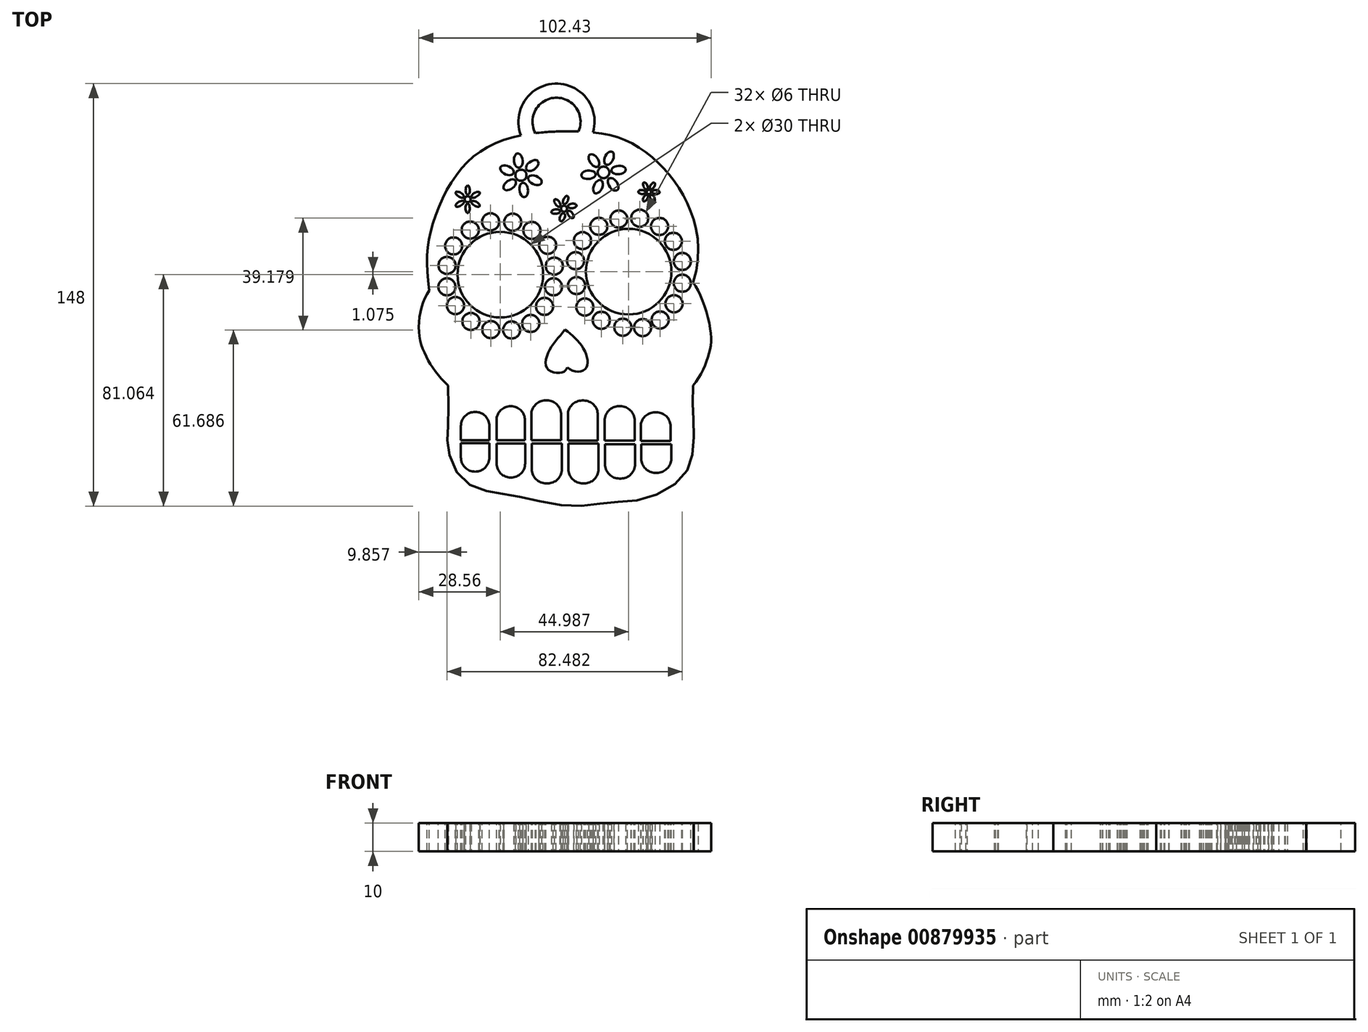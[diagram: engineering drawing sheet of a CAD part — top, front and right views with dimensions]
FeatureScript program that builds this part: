
annotation { "Feature Type Name" : "Feature", "Feature Type Description" : "" }
export const myFeature = defineFeature(function(context is Context, id is Id, definition is map)
    precondition{}
    {
        {
            var Q0;
            Q0=qCreatedBy(makeId("Top.planeOp"),FACE);
            var sketch = newSketch(context, id + "F0", { "sketchPlane" : qUnion([Q0])});
            skFitSpline(sketch, "E0", {"points": [v(-51.65, 30.7) * mm, v(-51.37, 50.55) * mm, v(-42.58, 70.68) * mm, v(-27.27, 82.88) * mm, v(-3.45, 86.56) * mm, v(15.55, 84.01) * mm, v(29.16, 74.94) * mm, v(39.37, 59.9) * mm, v(40.79, 33.54) * mm], "startDerivative": vector(-28.64, 201.5) * mm, "endDerivative": vector(-70.43, -226.16) * mm});
            skFitSpline(sketch, "E1", {"points": [v(-51.65, 30.7) * mm, v(-55.34, 17.94) * mm, v(-52.5, 7.17) * mm, v(-45.13, -2.47) * mm], "startDerivative": vector(-19.76, -24.65) * mm, "endDerivative": vector(28.6, -26.74) * mm});
            skFitSpline(sketch, "E2", {"points": [v(40.79, 33.54) * mm, v(46.74, 17.66) * mm, v(46.18, 8.02) * mm, v(40.79, -2.47) * mm], "startDerivative": vector(20.4, -25) * mm, "endDerivative": vector(-24.31, -27.97) * mm});
            skFitSpline(sketch, "E3", {"points": [v(-45.13, -2.47) * mm, v(-45.13, -17.5) * mm, v(-45.13, -24.6) * mm, v(-40.03, -35.37) * mm, v(-29.53, -39.9) * mm, v(-19.33, -41.6) * mm, v(-2.6, -44.72) * mm, v(10.73, -43.6) * mm, v(23.77, -42.17) * mm, v(37.1, -34.52) * mm, v(40.79, -24.88) * mm, v(40.79, -13.25) * mm, v(40.79, -2.47) * mm], "startDerivative": vector(7.8, -164.11) * mm, "endDerivative": vector(8.57, 179.66) * mm});
            skSolve(sketch);
        }
        {
            var Q0;
            Q0 = qSketchRegion(id + "F0", true);
            extrude(context, id + "F1", {"entities" : qUnion([Q0]), "oppositeDirection" : true, "depth" : 10 * mm, "offsetDistance" : 25.4 * mm});
        }
        {
            var Q0;
            Q0=makeQuery(id+"F1.opExtrude","CAP_FACE",FACE,{"disambiguationData":[OSD([sQuery(id+"F0.wireOp",EDGE,"E0"),sQuery(id+"F0.wireOp",EDGE,"E1"),sQuery(id+"F0.wireOp",EDGE,"E2"),sQuery(id+"F0.wireOp",EDGE,"E3")])],"isStart":true});
            var sketch = newSketch(context, id + "F2", { "sketchPlane" : qUnion([Q0])});
            skCircle(sketch, "E4", {"center": v(-26.78, 36.3) * mm, "radius": 15 * mm});
            skCircle(sketch, "E5", {"center": v(18.2, 37.38) * mm, "radius": 15 * mm});
            skSolve(sketch);
        }
        {
            var Q0;
            Q0 = qSketchRegion(id + "F2", true);
            extrude(context, id + "F3", {"entities" : qUnion([Q0]), "operationType" : NewBodyOperationType.REMOVE, "oppositeDirection" : true, "depth" : 20 * mm, "offsetDistance" : 25 * mm});
        }
        {
            var Q0;
            Q0=makeQuery(id+"F1.opExtrude","CAP_FACE",FACE,{"disambiguationData":[OSD([sQuery(id+"F0.wireOp",EDGE,"E0"),sQuery(id+"F0.wireOp",EDGE,"E1"),sQuery(id+"F0.wireOp",EDGE,"E2"),sQuery(id+"F0.wireOp",EDGE,"E3")])],"isStart":true});
            var sketch = newSketch(context, id + "F4", { "sketchPlane" : qUnion([Q0])});
            skLineSegment(sketch, "E6.bottom", {"start": v(-40.6, -11.76) * mm, "end": v(-30.6, -11.76) * mm});
            skLineSegment(sketch, "E6.top", {"start": v(-40.6, -21.76) * mm, "end": v(-30.6, -21.76) * mm});
            skLineSegment(sketch, "E6.left", {"start": v(-40.6, -11.76) * mm, "end": v(-40.6, -21.76) * mm});
            skLineSegment(sketch, "E6.right", {"start": v(-30.6, -11.76) * mm, "end": v(-30.6, -21.76) * mm});
            skSolve(sketch);
        }
        {
            var Q0;
            Q0 = qSketchRegion(id + "F4", true);
            extrude(context, id + "F5", {"entities" : qUnion([Q0]), "operationType" : NewBodyOperationType.REMOVE, "oppositeDirection" : true, "depth" : 20 * mm, "offsetDistance" : 25 * mm});
        }
        {
            var Q0;
            Q0=makeQuery(id+"F1.opExtrude","CAP_FACE",FACE,{"disambiguationData":[OSD([sQuery(id+"F0.wireOp",EDGE,"E0"),sQuery(id+"F0.wireOp",EDGE,"E1"),sQuery(id+"F0.wireOp",EDGE,"E2"),sQuery(id+"F0.wireOp",EDGE,"E3")])],"isStart":true});
            var sketch = newSketch(context, id + "F6", { "sketchPlane" : qUnion([Q0])});
            skLineSegment(sketch, "E7.bottom", {"start": v(-28.12, -9.76) * mm, "end": v(-18.12, -9.76) * mm});
            skLineSegment(sketch, "E7.top", {"start": v(-28.12, -21.76) * mm, "end": v(-18.12, -21.76) * mm});
            skLineSegment(sketch, "E7.left", {"start": v(-28.12, -9.76) * mm, "end": v(-28.12, -21.76) * mm});
            skLineSegment(sketch, "E7.right", {"start": v(-18.12, -9.76) * mm, "end": v(-18.12, -21.76) * mm});
            skSolve(sketch);
        }
        {
            var Q0;
            Q0 = qSketchRegion(id + "F6", true);
            extrude(context, id + "F7", {"entities" : qUnion([Q0]), "operationType" : NewBodyOperationType.REMOVE, "oppositeDirection" : true, "depth" : 20 * mm, "offsetDistance" : 25 * mm});
        }
        {
            var Q0;
            Q0=makeQuery(id+"F1.opExtrude","CAP_FACE",FACE,{"disambiguationData":[OSD([sQuery(id+"F0.wireOp",EDGE,"E0"),sQuery(id+"F0.wireOp",EDGE,"E1"),sQuery(id+"F0.wireOp",EDGE,"E2"),sQuery(id+"F0.wireOp",EDGE,"E3")])],"isStart":true});
            var sketch = newSketch(context, id + "F8", { "sketchPlane" : qUnion([Q0])});
            skLineSegment(sketch, "E8.bottom", {"start": v(-15.92, -7.76) * mm, "end": v(-5.42, -7.76) * mm});
            skLineSegment(sketch, "E8.top", {"start": v(-15.92, -21.76) * mm, "end": v(-5.42, -21.76) * mm});
            skLineSegment(sketch, "E8.left", {"start": v(-15.92, -7.76) * mm, "end": v(-15.92, -21.76) * mm});
            skLineSegment(sketch, "E8.right", {"start": v(-5.42, -7.76) * mm, "end": v(-5.42, -21.76) * mm});
            skSolve(sketch);
        }
        {
            var Q0;
            Q0 = qSketchRegion(id + "F8", true);
            extrude(context, id + "F9", {"entities" : qUnion([Q0]), "operationType" : NewBodyOperationType.REMOVE, "oppositeDirection" : true, "depth" : 20 * mm, "offsetDistance" : 25 * mm});
        }
        {
            var Q0;
            Q0=makeQuery(id+"F1.opExtrude","CAP_FACE",FACE,{"disambiguationData":[OSD([sQuery(id+"F0.wireOp",EDGE,"E0"),sQuery(id+"F0.wireOp",EDGE,"E1"),sQuery(id+"F0.wireOp",EDGE,"E2"),sQuery(id+"F0.wireOp",EDGE,"E3")])],"isStart":true});
            var sketch = newSketch(context, id + "F10", { "sketchPlane" : qUnion([Q0])});
            skLineSegment(sketch, "E9.bottom", {"start": v(-3.1, -7.78) * mm, "end": v(7.4, -7.78) * mm});
            skLineSegment(sketch, "E9.top", {"start": v(-3.1, -21.78) * mm, "end": v(7.4, -21.78) * mm});
            skLineSegment(sketch, "E9.left", {"start": v(-3.1, -7.78) * mm, "end": v(-3.1, -21.78) * mm});
            skLineSegment(sketch, "E9.right", {"start": v(7.4, -7.78) * mm, "end": v(7.4, -21.78) * mm});
            skSolve(sketch);
        }
        {
            var Q0;
            Q0 = qSketchRegion(id + "F10", true);
            extrude(context, id + "F11", {"entities" : qUnion([Q0]), "operationType" : NewBodyOperationType.REMOVE, "oppositeDirection" : true, "depth" : 20 * mm, "offsetDistance" : 25 * mm});
        }
        {
            var Q0;
            Q0=makeQuery(id+"F1.opExtrude","CAP_FACE",FACE,{"disambiguationData":[OSD([sQuery(id+"F0.wireOp",EDGE,"E0"),sQuery(id+"F0.wireOp",EDGE,"E1"),sQuery(id+"F0.wireOp",EDGE,"E2"),sQuery(id+"F0.wireOp",EDGE,"E3")])],"isStart":true});
            var sketch = newSketch(context, id + "F12", { "sketchPlane" : qUnion([Q0])});
            skPoint(sketch, "E10.oppositeSnap0", {"position": v(2.15, -21.78) * mm});
            skLineSegment(sketch, "E10.bottom", {"start": v(9.8, -9.78) * mm, "end": v(20.3, -9.78) * mm});
            skLineSegment(sketch, "E10.top", {"start": v(9.8, -21.78) * mm, "end": v(20.3, -21.78) * mm});
            skLineSegment(sketch, "E10.left", {"start": v(9.8, -9.78) * mm, "end": v(9.8, -21.78) * mm});
            skLineSegment(sketch, "E10.right", {"start": v(20.3, -9.78) * mm, "end": v(20.3, -21.78) * mm});
            skSolve(sketch);
        }
        {
            var Q0;
            Q0 = qSketchRegion(id + "F12", true);
            extrude(context, id + "F13", {"entities" : qUnion([Q0]), "operationType" : NewBodyOperationType.REMOVE, "oppositeDirection" : true, "depth" : 20 * mm, "offsetDistance" : 25 * mm});
        }
        {
            var Q0;
            Q0=makeQuery(id+"F1.opExtrude","CAP_FACE",FACE,{"disambiguationData":[OSD([sQuery(id+"F0.wireOp",EDGE,"E0"),sQuery(id+"F0.wireOp",EDGE,"E1"),sQuery(id+"F0.wireOp",EDGE,"E2"),sQuery(id+"F0.wireOp",EDGE,"E3")])],"isStart":true});
            var sketch = newSketch(context, id + "F14", { "sketchPlane" : qUnion([Q0])});
            skLineSegment(sketch, "E11.bottom", {"start": v(22.43, -11.91) * mm, "end": v(32.93, -11.91) * mm});
            skLineSegment(sketch, "E11.top", {"start": v(22.43, -21.91) * mm, "end": v(32.93, -21.91) * mm});
            skLineSegment(sketch, "E11.left", {"start": v(22.43, -11.91) * mm, "end": v(22.43, -21.91) * mm});
            skLineSegment(sketch, "E11.right", {"start": v(32.93, -11.91) * mm, "end": v(32.93, -21.91) * mm});
            skSolve(sketch);
        }
        {
            var Q0;
            Q0 = qSketchRegion(id + "F14", true);
            extrude(context, id + "F15", {"entities" : qUnion([Q0]), "operationType" : NewBodyOperationType.REMOVE, "oppositeDirection" : true, "depth" : 20 * mm, "offsetDistance" : 25 * mm});
        }
        {
            var Q0;
            Q0=makeQuery(id+"F1.opExtrude","CAP_FACE",FACE,{"disambiguationData":[OSD([sQuery(id+"F0.wireOp",EDGE,"E0"),sQuery(id+"F0.wireOp",EDGE,"E1"),sQuery(id+"F0.wireOp",EDGE,"E2"),sQuery(id+"F0.wireOp",EDGE,"E3")])],"isStart":true});
            var sketch = newSketch(context, id + "F16", { "sketchPlane" : qUnion([Q0])});
            skPoint(sketch, "E12.firstSnap0", {"position": v(-40.6, -16.76) * mm});
            skLineSegment(sketch, "E12.bottom", {"start": v(-40.6, -22.7) * mm, "end": v(-30.6, -22.7) * mm});
            skLineSegment(sketch, "E12.top", {"start": v(-40.6, -32.7) * mm, "end": v(-30.6, -32.7) * mm});
            skLineSegment(sketch, "E12.left", {"start": v(-40.6, -22.7) * mm, "end": v(-40.6, -32.7) * mm});
            skLineSegment(sketch, "E12.right", {"start": v(-30.6, -22.7) * mm, "end": v(-30.6, -32.7) * mm});
            skSolve(sketch);
        }
        {
            var Q0;
            Q0 = qSketchRegion(id + "F16", true);
            extrude(context, id + "F17", {"entities" : qUnion([Q0]), "operationType" : NewBodyOperationType.REMOVE, "oppositeDirection" : true, "depth" : 20 * mm, "offsetDistance" : 25 * mm});
        }
        {
            var Q0;
            Q0=makeQuery(id+"F1.opExtrude","CAP_FACE",FACE,{"disambiguationData":[OSD([sQuery(id+"F0.wireOp",EDGE,"E0"),sQuery(id+"F0.wireOp",EDGE,"E1"),sQuery(id+"F0.wireOp",EDGE,"E2"),sQuery(id+"F0.wireOp",EDGE,"E3")])],"isStart":true});
            var sketch = newSketch(context, id + "F18", { "sketchPlane" : qUnion([Q0])});
            skLineSegment(sketch, "E13.bottom", {"start": v(-28.07, -22.8) * mm, "end": v(-18.07, -22.8) * mm});
            skLineSegment(sketch, "E13.top", {"start": v(-28.07, -34.8) * mm, "end": v(-18.07, -34.8) * mm});
            skLineSegment(sketch, "E13.left", {"start": v(-28.07, -22.8) * mm, "end": v(-28.07, -34.8) * mm});
            skLineSegment(sketch, "E13.right", {"start": v(-18.07, -22.8) * mm, "end": v(-18.07, -34.8) * mm});
            skSolve(sketch);
        }
        {
            var Q0;
            Q0 = qSketchRegion(id + "F18", true);
            extrude(context, id + "F19", {"entities" : qUnion([Q0]), "operationType" : NewBodyOperationType.REMOVE, "oppositeDirection" : true, "depth" : 20 * mm, "offsetDistance" : 25 * mm});
        }
        {
            var Q0;
            Q0=makeQuery(id+"F1.opExtrude","CAP_FACE",FACE,{"disambiguationData":[OSD([sQuery(id+"F0.wireOp",EDGE,"E0"),sQuery(id+"F0.wireOp",EDGE,"E1"),sQuery(id+"F0.wireOp",EDGE,"E2"),sQuery(id+"F0.wireOp",EDGE,"E3")])],"isStart":true});
            var sketch = newSketch(context, id + "F20", { "sketchPlane" : qUnion([Q0])});
            skLineSegment(sketch, "E14.bottom", {"start": v(-15.7, -22.84) * mm, "end": v(-5.2, -22.84) * mm});
            skLineSegment(sketch, "E14.top", {"start": v(-15.7, -36.84) * mm, "end": v(-5.2, -36.84) * mm});
            skLineSegment(sketch, "E14.left", {"start": v(-15.7, -22.84) * mm, "end": v(-15.7, -36.84) * mm});
            skLineSegment(sketch, "E14.right", {"start": v(-5.2, -22.84) * mm, "end": v(-5.2, -36.84) * mm});
            skSolve(sketch);
        }
        {
            var Q0;
            Q0 = qSketchRegion(id + "F20", true);
            extrude(context, id + "F21", {"entities" : qUnion([Q0]), "operationType" : NewBodyOperationType.REMOVE, "oppositeDirection" : true, "depth" : 20 * mm, "offsetDistance" : 25 * mm});
        }
        {
            var Q0;
            Q0=makeQuery(id+"F1.opExtrude","CAP_FACE",FACE,{"disambiguationData":[OSD([sQuery(id+"F0.wireOp",EDGE,"E0"),sQuery(id+"F0.wireOp",EDGE,"E1"),sQuery(id+"F0.wireOp",EDGE,"E2"),sQuery(id+"F0.wireOp",EDGE,"E3")])],"isStart":true});
            var sketch = newSketch(context, id + "F22", { "sketchPlane" : qUnion([Q0])});
            skLineSegment(sketch, "E15.bottom", {"start": v(-2.88, -22.84) * mm, "end": v(7.62, -22.84) * mm});
            skLineSegment(sketch, "E15.top", {"start": v(-2.88, -36.84) * mm, "end": v(7.62, -36.84) * mm});
            skLineSegment(sketch, "E15.left", {"start": v(-2.88, -22.84) * mm, "end": v(-2.88, -36.84) * mm});
            skLineSegment(sketch, "E15.right", {"start": v(7.62, -22.84) * mm, "end": v(7.62, -36.84) * mm});
            skSolve(sketch);
        }
        {
            var Q0;
            Q0 = qSketchRegion(id + "F22", true);
            extrude(context, id + "F23", {"entities" : qUnion([Q0]), "operationType" : NewBodyOperationType.REMOVE, "oppositeDirection" : true, "depth" : 20 * mm, "offsetDistance" : 25 * mm});
        }
        {
            var Q0;
            Q0=makeQuery(id+"F1.opExtrude","CAP_FACE",FACE,{"disambiguationData":[OSD([sQuery(id+"F0.wireOp",EDGE,"E0"),sQuery(id+"F0.wireOp",EDGE,"E1"),sQuery(id+"F0.wireOp",EDGE,"E2"),sQuery(id+"F0.wireOp",EDGE,"E3")])],"isStart":true});
            var sketch = newSketch(context, id + "F24", { "sketchPlane" : qUnion([Q0])});
            skLineSegment(sketch, "E16.bottom", {"start": v(9.95, -23.12) * mm, "end": v(20.45, -23.12) * mm});
            skLineSegment(sketch, "E16.top", {"start": v(9.95, -35.12) * mm, "end": v(20.45, -35.12) * mm});
            skLineSegment(sketch, "E16.left", {"start": v(9.95, -23.12) * mm, "end": v(9.95, -35.12) * mm});
            skLineSegment(sketch, "E16.right", {"start": v(20.45, -23.12) * mm, "end": v(20.45, -35.12) * mm});
            skSolve(sketch);
        }
        {
            var Q0;
            Q0 = qSketchRegion(id + "F24", true);
            extrude(context, id + "F25", {"entities" : qUnion([Q0]), "operationType" : NewBodyOperationType.REMOVE, "oppositeDirection" : true, "depth" : 20 * mm, "offsetDistance" : 25 * mm});
        }
        {
            var Q0;
            Q0=makeQuery(id+"F1.opExtrude","CAP_FACE",FACE,{"disambiguationData":[OSD([sQuery(id+"F0.wireOp",EDGE,"E0"),sQuery(id+"F0.wireOp",EDGE,"E1"),sQuery(id+"F0.wireOp",EDGE,"E2"),sQuery(id+"F0.wireOp",EDGE,"E3")])],"isStart":true});
            var sketch = newSketch(context, id + "F26", { "sketchPlane" : qUnion([Q0])});
            skLineSegment(sketch, "E17.bottom", {"start": v(22.62, -23.12) * mm, "end": v(33.12, -23.12) * mm});
            skLineSegment(sketch, "E17.top", {"start": v(22.62, -33.12) * mm, "end": v(33.12, -33.12) * mm});
            skLineSegment(sketch, "E17.left", {"start": v(22.62, -23.12) * mm, "end": v(22.62, -33.12) * mm});
            skLineSegment(sketch, "E17.right", {"start": v(33.12, -23.12) * mm, "end": v(33.12, -33.12) * mm});
            skSolve(sketch);
        }
        {
            var Q0;
            Q0 = qSketchRegion(id + "F26", true);
            extrude(context, id + "F27", {"entities" : qUnion([Q0]), "operationType" : NewBodyOperationType.REMOVE, "oppositeDirection" : true, "depth" : 20 * mm, "offsetDistance" : 25 * mm});
        }
        {
            var Q0;
            Q0=makeQuery(id+"F1.opExtrude","CAP_FACE",FACE,{"disambiguationData":[OSD([sQuery(id+"F0.wireOp",EDGE,"E0"),sQuery(id+"F0.wireOp",EDGE,"E1"),sQuery(id+"F0.wireOp",EDGE,"E2"),sQuery(id+"F0.wireOp",EDGE,"E3")])],"isStart":true});
            var sketch = newSketch(context, id + "F28", { "sketchPlane" : qUnion([Q0])});
            skCircle(sketch, "E18", {"center": v(-37.33, 51.95) * mm, "radius": 3 * mm});
            skSolve(sketch);
        }
        {
            var Q0;
            Q0 = qSketchRegion(id + "F28", true);
            extrude(context, id + "F29", {"entities" : qUnion([Q0]), "operationType" : NewBodyOperationType.REMOVE, "oppositeDirection" : true, "depth" : 20 * mm, "offsetDistance" : 25 * mm});
        }
        {
            var Q0;
            Q0=makeQuery(id+"F1.opExtrude","CAP_FACE",FACE,{"disambiguationData":[OSD([sQuery(id+"F0.wireOp",EDGE,"E0"),sQuery(id+"F0.wireOp",EDGE,"E1"),sQuery(id+"F0.wireOp",EDGE,"E2"),sQuery(id+"F0.wireOp",EDGE,"E3")])],"isStart":true});
            var sketch = newSketch(context, id + "F30", { "sketchPlane" : qUnion([Q0])});
            skCircle(sketch, "E19", {"center": v(-30.18, 54.82) * mm, "radius": 3 * mm});
            skSolve(sketch);
        }
        {
            var Q0;
            Q0 = qSketchRegion(id + "F30", true);
            extrude(context, id + "F31", {"entities" : qUnion([Q0]), "operationType" : NewBodyOperationType.REMOVE, "oppositeDirection" : true, "depth" : 20 * mm, "offsetDistance" : 25 * mm});
        }
        {
            var Q0;
            Q0=makeQuery(id+"F1.opExtrude","CAP_FACE",FACE,{"disambiguationData":[OSD([sQuery(id+"F0.wireOp",EDGE,"E0"),sQuery(id+"F0.wireOp",EDGE,"E1"),sQuery(id+"F0.wireOp",EDGE,"E2"),sQuery(id+"F0.wireOp",EDGE,"E3")])],"isStart":true});
            var sketch = newSketch(context, id + "F32", { "sketchPlane" : qUnion([Q0])});
            skCircle(sketch, "E20", {"center": v(-22.43, 54.7) * mm, "radius": 3 * mm});
            skSolve(sketch);
        }
        {
            var Q0;
            Q0 = qSketchRegion(id + "F32", true);
            extrude(context, id + "F33", {"entities" : qUnion([Q0]), "operationType" : NewBodyOperationType.REMOVE, "oppositeDirection" : true, "depth" : 20 * mm, "offsetDistance" : 25 * mm});
        }
        {
            var Q0;
            Q0=makeQuery(id+"F1.opExtrude","CAP_FACE",FACE,{"disambiguationData":[OSD([sQuery(id+"F0.wireOp",EDGE,"E0"),sQuery(id+"F0.wireOp",EDGE,"E1"),sQuery(id+"F0.wireOp",EDGE,"E2"),sQuery(id+"F0.wireOp",EDGE,"E3")])],"isStart":true});
            var sketch = newSketch(context, id + "F34", { "sketchPlane" : qUnion([Q0])});
            skCircle(sketch, "E21", {"center": v(-15.72, 51.81) * mm, "radius": 3 * mm});
            skSolve(sketch);
        }
        {
            var Q0;
            Q0 = qSketchRegion(id + "F34", true);
            extrude(context, id + "F35", {"entities" : qUnion([Q0]), "operationType" : NewBodyOperationType.REMOVE, "oppositeDirection" : true, "depth" : 20 * mm, "offsetDistance" : 25 * mm});
        }
        {
            var Q0;
            Q0=makeQuery(id+"F1.opExtrude","CAP_FACE",FACE,{"disambiguationData":[OSD([sQuery(id+"F0.wireOp",EDGE,"E0"),sQuery(id+"F0.wireOp",EDGE,"E1"),sQuery(id+"F0.wireOp",EDGE,"E2"),sQuery(id+"F0.wireOp",EDGE,"E3")])],"isStart":true});
            var sketch = newSketch(context, id + "F36", { "sketchPlane" : qUnion([Q0])});
            skCircle(sketch, "E22", {"center": v(-43.14, 46.37) * mm, "radius": 3 * mm});
            skSolve(sketch);
        }
        {
            var Q0;
            Q0 = qSketchRegion(id + "F36", true);
            extrude(context, id + "F37", {"entities" : qUnion([Q0]), "operationType" : NewBodyOperationType.REMOVE, "oppositeDirection" : true, "depth" : 20 * mm, "offsetDistance" : 25 * mm});
        }
        {
            var Q0;
            Q0=makeQuery(id+"F1.opExtrude","CAP_FACE",FACE,{"disambiguationData":[OSD([sQuery(id+"F0.wireOp",EDGE,"E0"),sQuery(id+"F0.wireOp",EDGE,"E1"),sQuery(id+"F0.wireOp",EDGE,"E2"),sQuery(id+"F0.wireOp",EDGE,"E3")])],"isStart":true});
            var sketch = newSketch(context, id + "F38", { "sketchPlane" : qUnion([Q0])});
            skCircle(sketch, "E23", {"center": v(-45.45, 39.55) * mm, "radius": 3 * mm});
            skSolve(sketch);
        }
        {
            var Q0;
            Q0 = qSketchRegion(id + "F38", true);
            extrude(context, id + "F39", {"entities" : qUnion([Q0]), "operationType" : NewBodyOperationType.REMOVE, "oppositeDirection" : true, "depth" : 20 * mm, "offsetDistance" : 25 * mm});
        }
        {
            var Q0;
            Q0=makeQuery(id+"F1.opExtrude","CAP_FACE",FACE,{"disambiguationData":[OSD([sQuery(id+"F0.wireOp",EDGE,"E0"),sQuery(id+"F0.wireOp",EDGE,"E1"),sQuery(id+"F0.wireOp",EDGE,"E2"),sQuery(id+"F0.wireOp",EDGE,"E3")])],"isStart":true});
            var sketch = newSketch(context, id + "F40", { "sketchPlane" : qUnion([Q0])});
            skCircle(sketch, "E24", {"center": v(-10.17, 46.6) * mm, "radius": 3 * mm});
            skSolve(sketch);
        }
        {
            var Q0;
            Q0 = qSketchRegion(id + "F40", true);
            extrude(context, id + "F41", {"entities" : qUnion([Q0]), "operationType" : NewBodyOperationType.REMOVE, "oppositeDirection" : true, "depth" : 20 * mm, "offsetDistance" : 25 * mm});
        }
        {
            var Q0;
            Q0=makeQuery(id+"F1.opExtrude","CAP_FACE",FACE,{"disambiguationData":[OSD([sQuery(id+"F0.wireOp",EDGE,"E0"),sQuery(id+"F0.wireOp",EDGE,"E1"),sQuery(id+"F0.wireOp",EDGE,"E2"),sQuery(id+"F0.wireOp",EDGE,"E3")])],"isStart":true});
            var sketch = newSketch(context, id + "F42", { "sketchPlane" : qUnion([Q0])});
            skCircle(sketch, "E25", {"center": v(-7.85, 39.3) * mm, "radius": 3 * mm});
            skSolve(sketch);
        }
        {
            var Q0;
            Q0 = qSketchRegion(id + "F42", true);
            extrude(context, id + "F43", {"entities" : qUnion([Q0]), "operationType" : NewBodyOperationType.REMOVE, "oppositeDirection" : true, "depth" : 20 * mm, "offsetDistance" : 25 * mm});
        }
        {
            var Q0;
            Q0=makeQuery(id+"F1.opExtrude","CAP_FACE",FACE,{"disambiguationData":[OSD([sQuery(id+"F0.wireOp",EDGE,"E0"),sQuery(id+"F0.wireOp",EDGE,"E1"),sQuery(id+"F0.wireOp",EDGE,"E2"),sQuery(id+"F0.wireOp",EDGE,"E3")])],"isStart":true});
            var sketch = newSketch(context, id + "F44", { "sketchPlane" : qUnion([Q0])});
            skCircle(sketch, "E26", {"center": v(-45.48, 32.04) * mm, "radius": 3 * mm});
            skSolve(sketch);
        }
        {
            var Q0;
            Q0 = qSketchRegion(id + "F44", true);
            extrude(context, id + "F45", {"entities" : qUnion([Q0]), "operationType" : NewBodyOperationType.REMOVE, "oppositeDirection" : true, "depth" : 20 * mm, "offsetDistance" : 25 * mm});
        }
        {
            var Q0;
            Q0=makeQuery(id+"F1.opExtrude","CAP_FACE",FACE,{"disambiguationData":[OSD([sQuery(id+"F0.wireOp",EDGE,"E0"),sQuery(id+"F0.wireOp",EDGE,"E1"),sQuery(id+"F0.wireOp",EDGE,"E2"),sQuery(id+"F0.wireOp",EDGE,"E3")])],"isStart":true});
            var sketch = newSketch(context, id + "F46", { "sketchPlane" : qUnion([Q0])});
            skCircle(sketch, "E27", {"center": v(-42.49, 25.48) * mm, "radius": 3 * mm});
            skSolve(sketch);
        }
        {
            var Q0;
            Q0 = qSketchRegion(id + "F46", true);
            extrude(context, id + "F47", {"entities" : qUnion([Q0]), "operationType" : NewBodyOperationType.REMOVE, "oppositeDirection" : true, "depth" : 20 * mm, "offsetDistance" : 25 * mm});
        }
        {
            var Q0;
            Q0=makeQuery(id+"F1.opExtrude","CAP_FACE",FACE,{"disambiguationData":[OSD([sQuery(id+"F0.wireOp",EDGE,"E0"),sQuery(id+"F0.wireOp",EDGE,"E1"),sQuery(id+"F0.wireOp",EDGE,"E2"),sQuery(id+"F0.wireOp",EDGE,"E3")])],"isStart":true});
            var sketch = newSketch(context, id + "F48", { "sketchPlane" : qUnion([Q0])});
            skCircle(sketch, "E28", {"center": v(-8.14, 32.04) * mm, "radius": 3 * mm});
            skSolve(sketch);
        }
        {
            var Q0;
            Q0 = qSketchRegion(id + "F48", true);
            extrude(context, id + "F49", {"entities" : qUnion([Q0]), "operationType" : NewBodyOperationType.REMOVE, "oppositeDirection" : true, "depth" : 20 * mm, "offsetDistance" : 25 * mm});
        }
        {
            var Q0;
            Q0=makeQuery(id+"F1.opExtrude","CAP_FACE",FACE,{"disambiguationData":[OSD([sQuery(id+"F0.wireOp",EDGE,"E0"),sQuery(id+"F0.wireOp",EDGE,"E1"),sQuery(id+"F0.wireOp",EDGE,"E2"),sQuery(id+"F0.wireOp",EDGE,"E3")])],"isStart":true});
            var sketch = newSketch(context, id + "F50", { "sketchPlane" : qUnion([Q0])});
            skCircle(sketch, "E29", {"center": v(-11.27, 25.2) * mm, "radius": 3 * mm});
            skSolve(sketch);
        }
        {
            var Q0;
            Q0 = qSketchRegion(id + "F50", true);
            extrude(context, id + "F51", {"entities" : qUnion([Q0]), "operationType" : NewBodyOperationType.REMOVE, "oppositeDirection" : true, "depth" : 20 * mm, "offsetDistance" : 25 * mm});
        }
        {
            var Q0;
            Q0=makeQuery(id+"F1.opExtrude","CAP_FACE",FACE,{"disambiguationData":[OSD([sQuery(id+"F0.wireOp",EDGE,"E0"),sQuery(id+"F0.wireOp",EDGE,"E1"),sQuery(id+"F0.wireOp",EDGE,"E2"),sQuery(id+"F0.wireOp",EDGE,"E3")])],"isStart":true});
            var sketch = newSketch(context, id + "F52", { "sketchPlane" : qUnion([Q0])});
            skCircle(sketch, "E30", {"center": v(-37.07, 19.92) * mm, "radius": 3 * mm});
            skSolve(sketch);
        }
        {
            var Q0;
            Q0 = qSketchRegion(id + "F52", true);
            extrude(context, id + "F53", {"entities" : qUnion([Q0]), "operationType" : NewBodyOperationType.REMOVE, "oppositeDirection" : true, "depth" : 20 * mm, "offsetDistance" : 25 * mm});
        }
        {
            var Q0;
            Q0=makeQuery(id+"F1.opExtrude","CAP_FACE",FACE,{"disambiguationData":[OSD([sQuery(id+"F0.wireOp",EDGE,"E0"),sQuery(id+"F0.wireOp",EDGE,"E1"),sQuery(id+"F0.wireOp",EDGE,"E2"),sQuery(id+"F0.wireOp",EDGE,"E3")])],"isStart":true});
            var sketch = newSketch(context, id + "F54", { "sketchPlane" : qUnion([Q0])});
            skCircle(sketch, "E31", {"center": v(-30.09, 17.07) * mm, "radius": 3 * mm});
            skSolve(sketch);
        }
        {
            var Q0;
            Q0 = qSketchRegion(id + "F54", true);
            extrude(context, id + "F55", {"entities" : qUnion([Q0]), "operationType" : NewBodyOperationType.REMOVE, "oppositeDirection" : true, "depth" : 20 * mm, "offsetDistance" : 25 * mm});
        }
        {
            var Q0;
            Q0=makeQuery(id+"F1.opExtrude","CAP_FACE",FACE,{"disambiguationData":[OSD([sQuery(id+"F0.wireOp",EDGE,"E0"),sQuery(id+"F0.wireOp",EDGE,"E1"),sQuery(id+"F0.wireOp",EDGE,"E2"),sQuery(id+"F0.wireOp",EDGE,"E3")])],"isStart":true});
            var sketch = newSketch(context, id + "F56", { "sketchPlane" : qUnion([Q0])});
            skCircle(sketch, "E32", {"center": v(-16.12, 19.2) * mm, "radius": 3 * mm});
            skSolve(sketch);
        }
        {
            var Q0;
            Q0 = qSketchRegion(id + "F56", true);
            extrude(context, id + "F57", {"entities" : qUnion([Q0]), "operationType" : NewBodyOperationType.REMOVE, "oppositeDirection" : true, "depth" : 20 * mm, "offsetDistance" : 25 * mm});
        }
        {
            var Q0;
            Q0=makeQuery(id+"F1.opExtrude","CAP_FACE",FACE,{"disambiguationData":[OSD([sQuery(id+"F0.wireOp",EDGE,"E0"),sQuery(id+"F0.wireOp",EDGE,"E1"),sQuery(id+"F0.wireOp",EDGE,"E2"),sQuery(id+"F0.wireOp",EDGE,"E3")])],"isStart":true});
            var sketch = newSketch(context, id + "F58", { "sketchPlane" : qUnion([Q0])});
            skCircle(sketch, "E33", {"center": v(-22.82, 16.93) * mm, "radius": 3 * mm});
            skSolve(sketch);
        }
        {
            var Q0;
            Q0 = qSketchRegion(id + "F58", true);
            extrude(context, id + "F59", {"entities" : qUnion([Q0]), "operationType" : NewBodyOperationType.REMOVE, "oppositeDirection" : true, "depth" : 20 * mm, "offsetDistance" : 25 * mm});
        }
        {
            var Q0;
            Q0=makeQuery(id+"F1.opExtrude","CAP_FACE",FACE,{"disambiguationData":[OSD([sQuery(id+"F0.wireOp",EDGE,"E0"),sQuery(id+"F0.wireOp",EDGE,"E1"),sQuery(id+"F0.wireOp",EDGE,"E2"),sQuery(id+"F0.wireOp",EDGE,"E3")])],"isStart":true});
            var sketch = newSketch(context, id + "F60", { "sketchPlane" : qUnion([Q0])});
            skCircle(sketch, "E34", {"center": v(14.76, 55.79) * mm, "radius": 3 * mm});
            skSolve(sketch);
        }
        {
            var Q0;
            Q0 = qSketchRegion(id + "F60", true);
            extrude(context, id + "F61", {"entities" : qUnion([Q0]), "operationType" : NewBodyOperationType.REMOVE, "oppositeDirection" : true, "depth" : 20 * mm, "offsetDistance" : 25 * mm});
        }
        {
            var Q0;
            Q0=makeQuery(id+"F1.opExtrude","CAP_FACE",FACE,{"disambiguationData":[OSD([sQuery(id+"F0.wireOp",EDGE,"E0"),sQuery(id+"F0.wireOp",EDGE,"E1"),sQuery(id+"F0.wireOp",EDGE,"E2"),sQuery(id+"F0.wireOp",EDGE,"E3")])],"isStart":true});
            var sketch = newSketch(context, id + "F62", { "sketchPlane" : qUnion([Q0])});
            skCircle(sketch, "E35", {"center": v(7.75, 53.24) * mm, "radius": 3 * mm});
            skSolve(sketch);
        }
        {
            var Q0;
            Q0 = qSketchRegion(id + "F62", true);
            extrude(context, id + "F63", {"entities" : qUnion([Q0]), "operationType" : NewBodyOperationType.REMOVE, "oppositeDirection" : true, "depth" : 20 * mm, "offsetDistance" : 25 * mm});
        }
        {
            var Q0;
            Q0=makeQuery(id+"F1.opExtrude","CAP_FACE",FACE,{"disambiguationData":[OSD([sQuery(id+"F0.wireOp",EDGE,"E0"),sQuery(id+"F0.wireOp",EDGE,"E1"),sQuery(id+"F0.wireOp",EDGE,"E2"),sQuery(id+"F0.wireOp",EDGE,"E3")])],"isStart":true});
            var sketch = newSketch(context, id + "F64", { "sketchPlane" : qUnion([Q0])});
            skCircle(sketch, "E36", {"center": v(22.08, 56.1) * mm, "radius": 3 * mm});
            skSolve(sketch);
        }
        {
            var Q0;
            Q0 = qSketchRegion(id + "F64", true);
            extrude(context, id + "F65", {"entities" : qUnion([Q0]), "operationType" : NewBodyOperationType.REMOVE, "oppositeDirection" : true, "depth" : 20 * mm, "offsetDistance" : 25 * mm});
        }
        {
            var Q0;
            Q0=makeQuery(id+"F1.opExtrude","CAP_FACE",FACE,{"disambiguationData":[OSD([sQuery(id+"F0.wireOp",EDGE,"E0"),sQuery(id+"F0.wireOp",EDGE,"E1"),sQuery(id+"F0.wireOp",EDGE,"E2"),sQuery(id+"F0.wireOp",EDGE,"E3")])],"isStart":true});
            var sketch = newSketch(context, id + "F66", { "sketchPlane" : qUnion([Q0])});
            skCircle(sketch, "E37", {"center": v(29.01, 53.21) * mm, "radius": 3 * mm});
            skSolve(sketch);
        }
        {
            var Q0;
            Q0 = qSketchRegion(id + "F66", true);
            extrude(context, id + "F67", {"entities" : qUnion([Q0]), "operationType" : NewBodyOperationType.REMOVE, "oppositeDirection" : true, "depth" : 20 * mm, "offsetDistance" : 25 * mm});
        }
        {
            var Q0;
            Q0=makeQuery(id+"F1.opExtrude","CAP_FACE",FACE,{"disambiguationData":[OSD([sQuery(id+"F0.wireOp",EDGE,"E0"),sQuery(id+"F0.wireOp",EDGE,"E1"),sQuery(id+"F0.wireOp",EDGE,"E2"),sQuery(id+"F0.wireOp",EDGE,"E3")])],"isStart":true});
            var sketch = newSketch(context, id + "F68", { "sketchPlane" : qUnion([Q0])});
            skCircle(sketch, "E38", {"center": v(2.03, 48.23) * mm, "radius": 3 * mm});
            skSolve(sketch);
        }
        {
            var Q0;
            Q0 = qSketchRegion(id + "F68", true);
            extrude(context, id + "F69", {"entities" : qUnion([Q0]), "operationType" : NewBodyOperationType.REMOVE, "oppositeDirection" : true, "depth" : 20 * mm, "offsetDistance" : 25 * mm});
        }
        {
            var Q0;
            Q0=makeQuery(id+"F1.opExtrude","CAP_FACE",FACE,{"disambiguationData":[OSD([sQuery(id+"F0.wireOp",EDGE,"E0"),sQuery(id+"F0.wireOp",EDGE,"E1"),sQuery(id+"F0.wireOp",EDGE,"E2"),sQuery(id+"F0.wireOp",EDGE,"E3")])],"isStart":true});
            var sketch = newSketch(context, id + "F70", { "sketchPlane" : qUnion([Q0])});
            skCircle(sketch, "E39", {"center": v(-0.4, 41.17) * mm, "radius": 3 * mm});
            skSolve(sketch);
        }
        {
            var Q0;
            Q0 = qSketchRegion(id + "F70", true);
            extrude(context, id + "F71", {"entities" : qUnion([Q0]), "operationType" : NewBodyOperationType.REMOVE, "oppositeDirection" : true, "depth" : 20 * mm, "offsetDistance" : 25 * mm});
        }
        {
            var Q0;
            Q0=makeQuery(id+"F1.opExtrude","CAP_FACE",FACE,{"disambiguationData":[OSD([sQuery(id+"F0.wireOp",EDGE,"E0"),sQuery(id+"F0.wireOp",EDGE,"E1"),sQuery(id+"F0.wireOp",EDGE,"E2"),sQuery(id+"F0.wireOp",EDGE,"E3")])],"isStart":true});
            var sketch = newSketch(context, id + "F72", { "sketchPlane" : qUnion([Q0])});
            skCircle(sketch, "E40", {"center": v(33.87, 48) * mm, "radius": 3 * mm});
            skSolve(sketch);
        }
        {
            var Q0;
            Q0 = qSketchRegion(id + "F72", true);
            extrude(context, id + "F73", {"entities" : qUnion([Q0]), "operationType" : NewBodyOperationType.REMOVE, "oppositeDirection" : true, "depth" : 20 * mm, "offsetDistance" : 25 * mm});
        }
        {
            var Q0;
            Q0=makeQuery(id+"F1.opExtrude","CAP_FACE",FACE,{"disambiguationData":[OSD([sQuery(id+"F0.wireOp",EDGE,"E0"),sQuery(id+"F0.wireOp",EDGE,"E1"),sQuery(id+"F0.wireOp",EDGE,"E2"),sQuery(id+"F0.wireOp",EDGE,"E3")])],"isStart":true});
            var sketch = newSketch(context, id + "F74", { "sketchPlane" : qUnion([Q0])});
            skCircle(sketch, "E41", {"center": v(37, 40.94) * mm, "radius": 3 * mm});
            skSolve(sketch);
        }
        {
            var Q0;
            Q0 = qSketchRegion(id + "F74", true);
            extrude(context, id + "F75", {"entities" : qUnion([Q0]), "operationType" : NewBodyOperationType.REMOVE, "oppositeDirection" : true, "depth" : 20 * mm, "offsetDistance" : 25 * mm});
        }
        {
            var Q0;
            Q0=makeQuery(id+"F1.opExtrude","CAP_FACE",FACE,{"disambiguationData":[OSD([sQuery(id+"F0.wireOp",EDGE,"E0"),sQuery(id+"F0.wireOp",EDGE,"E1"),sQuery(id+"F0.wireOp",EDGE,"E2"),sQuery(id+"F0.wireOp",EDGE,"E3")])],"isStart":true});
            var sketch = newSketch(context, id + "F76", { "sketchPlane" : qUnion([Q0])});
            skCircle(sketch, "E42", {"center": v(-0.05, 32.49) * mm, "radius": 3 * mm});
            skSolve(sketch);
        }
        {
            var Q0;
            Q0 = qSketchRegion(id + "F76", true);
            extrude(context, id + "F77", {"entities" : qUnion([Q0]), "operationType" : NewBodyOperationType.REMOVE, "oppositeDirection" : true, "depth" : 20 * mm, "offsetDistance" : 25 * mm});
        }
        {
            var Q0;
            Q0=makeQuery(id+"F1.opExtrude","CAP_FACE",FACE,{"disambiguationData":[OSD([sQuery(id+"F0.wireOp",EDGE,"E0"),sQuery(id+"F0.wireOp",EDGE,"E1"),sQuery(id+"F0.wireOp",EDGE,"E2"),sQuery(id+"F0.wireOp",EDGE,"E3")])],"isStart":true});
            var sketch = newSketch(context, id + "F78", { "sketchPlane" : qUnion([Q0])});
            skCircle(sketch, "E43", {"center": v(2.84, 24.96) * mm, "radius": 3 * mm});
            skSolve(sketch);
        }
        {
            var Q0;
            Q0 = qSketchRegion(id + "F78", true);
            extrude(context, id + "F79", {"entities" : qUnion([Q0]), "operationType" : NewBodyOperationType.REMOVE, "oppositeDirection" : true, "depth" : 20 * mm, "offsetDistance" : 25 * mm});
        }
        {
            var Q0;
            Q0=makeQuery(id+"F1.opExtrude","CAP_FACE",FACE,{"disambiguationData":[OSD([sQuery(id+"F0.wireOp",EDGE,"E0"),sQuery(id+"F0.wireOp",EDGE,"E1"),sQuery(id+"F0.wireOp",EDGE,"E2"),sQuery(id+"F0.wireOp",EDGE,"E3")])],"isStart":true});
            var sketch = newSketch(context, id + "F80", { "sketchPlane" : qUnion([Q0])});
            skCircle(sketch, "E44", {"center": v(37, 33.3) * mm, "radius": 3 * mm});
            skSolve(sketch);
        }
        {
            var Q0;
            Q0 = qSketchRegion(id + "F80", true);
            extrude(context, id + "F81", {"entities" : qUnion([Q0]), "operationType" : NewBodyOperationType.REMOVE, "oppositeDirection" : true, "depth" : 20 * mm, "offsetDistance" : 25 * mm});
        }
        {
            var Q0;
            Q0=makeQuery(id+"F1.opExtrude","CAP_FACE",FACE,{"disambiguationData":[OSD([sQuery(id+"F0.wireOp",EDGE,"E0"),sQuery(id+"F0.wireOp",EDGE,"E1"),sQuery(id+"F0.wireOp",EDGE,"E2"),sQuery(id+"F0.wireOp",EDGE,"E3")])],"isStart":true});
            var sketch = newSketch(context, id + "F82", { "sketchPlane" : qUnion([Q0])});
            skCircle(sketch, "E45", {"center": v(34.1, 26.12) * mm, "radius": 3 * mm});
            skSolve(sketch);
        }
        {
            var Q0;
            Q0 = qSketchRegion(id + "F82", true);
            extrude(context, id + "F83", {"entities" : qUnion([Q0]), "operationType" : NewBodyOperationType.REMOVE, "oppositeDirection" : true, "depth" : 20 * mm, "offsetDistance" : 25 * mm});
        }
        {
            var Q0;
            Q0=makeQuery(id+"F1.opExtrude","CAP_FACE",FACE,{"disambiguationData":[OSD([sQuery(id+"F0.wireOp",EDGE,"E0"),sQuery(id+"F0.wireOp",EDGE,"E1"),sQuery(id+"F0.wireOp",EDGE,"E2"),sQuery(id+"F0.wireOp",EDGE,"E3")])],"isStart":true});
            var sketch = newSketch(context, id + "F84", { "sketchPlane" : qUnion([Q0])});
            skCircle(sketch, "E46", {"center": v(8.63, 20.33) * mm, "radius": 3 * mm});
            skSolve(sketch);
        }
        {
            var Q0;
            Q0 = qSketchRegion(id + "F84", true);
            extrude(context, id + "F85", {"entities" : qUnion([Q0]), "operationType" : NewBodyOperationType.REMOVE, "oppositeDirection" : true, "depth" : 20 * mm, "offsetDistance" : 25 * mm});
        }
        {
            var Q0;
            Q0=makeQuery(id+"F1.opExtrude","CAP_FACE",FACE,{"disambiguationData":[OSD([sQuery(id+"F0.wireOp",EDGE,"E0"),sQuery(id+"F0.wireOp",EDGE,"E1"),sQuery(id+"F0.wireOp",EDGE,"E2"),sQuery(id+"F0.wireOp",EDGE,"E3")])],"isStart":true});
            var sketch = newSketch(context, id + "F86", { "sketchPlane" : qUnion([Q0])});
            skCircle(sketch, "E47", {"center": v(16.16, 17.9) * mm, "radius": 3 * mm});
            skSolve(sketch);
        }
        {
            var Q0;
            Q0 = qSketchRegion(id + "F86", true);
            extrude(context, id + "F87", {"entities" : qUnion([Q0]), "operationType" : NewBodyOperationType.REMOVE, "oppositeDirection" : true, "depth" : 20 * mm, "offsetDistance" : 25 * mm});
        }
        {
            var Q0;
            Q0=makeQuery(id+"F1.opExtrude","CAP_FACE",FACE,{"disambiguationData":[OSD([sQuery(id+"F0.wireOp",EDGE,"E0"),sQuery(id+"F0.wireOp",EDGE,"E1"),sQuery(id+"F0.wireOp",EDGE,"E2"),sQuery(id+"F0.wireOp",EDGE,"E3")])],"isStart":true});
            var sketch = newSketch(context, id + "F88", { "sketchPlane" : qUnion([Q0])});
            skCircle(sketch, "E48", {"center": v(29.24, 20.45) * mm, "radius": 3 * mm});
            skSolve(sketch);
        }
        {
            var Q0;
            Q0 = qSketchRegion(id + "F88", true);
            extrude(context, id + "F89", {"entities" : qUnion([Q0]), "operationType" : NewBodyOperationType.REMOVE, "oppositeDirection" : true, "depth" : 20 * mm, "offsetDistance" : 25 * mm});
        }
        {
            var Q0;
            Q0=makeQuery(id+"F1.opExtrude","CAP_FACE",FACE,{"disambiguationData":[OSD([sQuery(id+"F0.wireOp",EDGE,"E0"),sQuery(id+"F0.wireOp",EDGE,"E1"),sQuery(id+"F0.wireOp",EDGE,"E2"),sQuery(id+"F0.wireOp",EDGE,"E3")])],"isStart":true});
            var sketch = newSketch(context, id + "F90", { "sketchPlane" : qUnion([Q0])});
            skCircle(sketch, "E49", {"center": v(23.1, 17.78) * mm, "radius": 3 * mm});
            skSolve(sketch);
        }
        {
            var Q0;
            Q0 = qSketchRegion(id + "F90", true);
            extrude(context, id + "F91", {"entities" : qUnion([Q0]), "operationType" : NewBodyOperationType.REMOVE, "oppositeDirection" : true, "depth" : 20 * mm, "offsetDistance" : 25 * mm});
        }
        {
            var Q0;
            Q0=makeQuery(id+"F1.opExtrude","CAP_FACE",FACE,{"disambiguationData":[OSD([sQuery(id+"F0.wireOp",EDGE,"E0"),sQuery(id+"F0.wireOp",EDGE,"E1"),sQuery(id+"F0.wireOp",EDGE,"E2"),sQuery(id+"F0.wireOp",EDGE,"E3")])],"isStart":true});
            var sketch = newSketch(context, id + "F92", { "sketchPlane" : qUnion([Q0])});
            skFitSpline(sketch, "E50", {"points": [v(-4.16, 17.06) * mm, v(-9.75, 9.47) * mm, v(-10.15, 3.22) * mm, v(-5.07, 2.05) * mm, v(-3.24, 3.87) * mm], "startDerivative": vector(-17.6, -23.33) * mm, "endDerivative": vector(7.19, 13.02) * mm});
            skPoint(sketch, "E51.1.internal.orphan", {"position": v(2.88, 9.47) * mm});
            skPoint(sketch, "E51.2.internal.orphan", {"position": v(5.09, 3.14) * mm});
            skPoint(sketch, "E51.3.internal.orphan", {"position": v(2.22, 2.05) * mm});
            skFitSpline(sketch, "E52", {"points": [v(-4.16, 17.06) * mm, v(2.88, 9.47) * mm, v(2.88, 3.14) * mm, v(-3.24, 3.87) * mm], "startDerivative": vector(21.3, -15.9) * mm, "endDerivative": vector(-16.83, 19.06) * mm});
            skSolve(sketch);
        }
        {
            var Q0;
            Q0 = qSketchRegion(id + "F92", true);
            extrude(context, id + "F93", {"entities" : qUnion([Q0]), "operationType" : NewBodyOperationType.REMOVE, "oppositeDirection" : true, "depth" : 20 * mm, "offsetDistance" : 25 * mm});
        }
        {
            var Q0;
            Q0=makeQuery(id+"F1.opExtrude","CAP_FACE",FACE,{"disambiguationData":[OSD([sQuery(id+"F0.wireOp",EDGE,"E0"),sQuery(id+"F0.wireOp",EDGE,"E1"),sQuery(id+"F0.wireOp",EDGE,"E2"),sQuery(id+"F0.wireOp",EDGE,"E3")])],"isStart":true});
            var sketch = newSketch(context, id + "F94", { "sketchPlane" : qUnion([Q0])});
            skCircle(sketch, "E53", {"center": v(-7.08, 89.9) * mm, "radius": 13.35 * mm});
            skCircle(sketch, "E54", {"center": v(-7.08, 89.9) * mm, "radius": 8.43 * mm});
            skSolve(sketch);
        }
        {
            var Q0;
            Q0 = qSketchRegion(id + "F94", true);
            var Q1;
            Q1=makeQuery(id+"F1.opExtrude","CAP_FACE",FACE,{"disambiguationData":[OSD([sQuery(id+"F0.wireOp",EDGE,"E0"),sQuery(id+"F0.wireOp",EDGE,"E1"),sQuery(id+"F0.wireOp",EDGE,"E2"),sQuery(id+"F0.wireOp",EDGE,"E3")])],"isStart":false});
            extrude(context, id + "F95", {"entities" : qUnion([Q0]), "operationType" : NewBodyOperationType.ADD, "endBound" : BoundingType.UP_TO_SURFACE, "oppositeDirection" : true, "depth" : 5 * mm, "endBoundEntityFace" : qUnion([Q1]), "offsetDistance" : 25 * mm});
        }
        {
            var Q0;
            Q0=makeQuery(id+"F5.boolean.opBoolean","COPY",EDGE,{"derivedFrom":makeQuery(id+"F5.opExtrude","SWEPT_EDGE",EDGE,{"disambiguationData":[OSD([sQuery(id+"F4.wireOp",EDGE,"E6.bottom"),sQuery(id+"F4.wireOp",EDGE,"E6.right")])]})});
            var Q1;
            Q1=makeQuery(id+"F5.boolean.opBoolean","COPY",EDGE,{"derivedFrom":makeQuery(id+"F5.opExtrude","SWEPT_EDGE",EDGE,{"disambiguationData":[OSD([sQuery(id+"F4.wireOp",EDGE,"E6.bottom"),sQuery(id+"F4.wireOp",EDGE,"E6.left")])]})});
            var Q2;
            Q2=makeQuery(id+"F7.boolean.opBoolean","COPY",EDGE,{"derivedFrom":makeQuery(id+"F7.opExtrude","SWEPT_EDGE",EDGE,{"disambiguationData":[OSD([sQuery(id+"F6.wireOp",EDGE,"E7.bottom"),sQuery(id+"F6.wireOp",EDGE,"E7.left")])]})});
            var Q3;
            Q3=makeQuery(id+"F7.boolean.opBoolean","COPY",EDGE,{"derivedFrom":makeQuery(id+"F7.opExtrude","SWEPT_EDGE",EDGE,{"disambiguationData":[OSD([sQuery(id+"F6.wireOp",EDGE,"E7.bottom"),sQuery(id+"F6.wireOp",EDGE,"E7.right")])]})});
            var Q4;
            Q4=makeQuery(id+"F9.boolean.opBoolean","COPY",EDGE,{"derivedFrom":makeQuery(id+"F9.opExtrude","SWEPT_EDGE",EDGE,{"disambiguationData":[OSD([sQuery(id+"F8.wireOp",EDGE,"E8.bottom"),sQuery(id+"F8.wireOp",EDGE,"E8.right")])]})});
            var Q5;
            Q5=makeQuery(id+"F11.boolean.opBoolean","COPY",EDGE,{"derivedFrom":makeQuery(id+"F11.opExtrude","SWEPT_EDGE",EDGE,{"disambiguationData":[OSD([sQuery(id+"F10.wireOp",EDGE,"E9.bottom"),sQuery(id+"F10.wireOp",EDGE,"E9.right")])]})});
            var Q6;
            Q6=makeQuery(id+"F13.boolean.opBoolean","COPY",EDGE,{"derivedFrom":makeQuery(id+"F13.opExtrude","SWEPT_EDGE",EDGE,{"disambiguationData":[OSD([sQuery(id+"F12.wireOp",EDGE,"E10.bottom"),sQuery(id+"F12.wireOp",EDGE,"E10.right")])]})});
            var Q7;
            Q7=makeQuery(id+"F15.boolean.opBoolean","COPY",EDGE,{"derivedFrom":makeQuery(id+"F15.opExtrude","SWEPT_EDGE",EDGE,{"disambiguationData":[OSD([sQuery(id+"F14.wireOp",EDGE,"E11.bottom"),sQuery(id+"F14.wireOp",EDGE,"E11.right")])]})});
            var Q8;
            Q8=makeQuery(id+"F9.boolean.opBoolean","COPY",EDGE,{"derivedFrom":makeQuery(id+"F9.opExtrude","SWEPT_EDGE",EDGE,{"disambiguationData":[OSD([sQuery(id+"F8.wireOp",EDGE,"E8.bottom"),sQuery(id+"F8.wireOp",EDGE,"E8.left")])]})});
            var Q9;
            Q9=makeQuery(id+"F13.boolean.opBoolean","COPY",EDGE,{"derivedFrom":makeQuery(id+"F13.opExtrude","SWEPT_EDGE",EDGE,{"disambiguationData":[OSD([sQuery(id+"F12.wireOp",EDGE,"E10.bottom"),sQuery(id+"F12.wireOp",EDGE,"E10.left")])]})});
            var Q10;
            Q10=makeQuery(id+"F15.boolean.opBoolean","COPY",EDGE,{"derivedFrom":makeQuery(id+"F15.opExtrude","SWEPT_EDGE",EDGE,{"disambiguationData":[OSD([sQuery(id+"F14.wireOp",EDGE,"E11.bottom"),sQuery(id+"F14.wireOp",EDGE,"E11.left")])]})});
            var Q11;
            Q11=makeQuery(id+"F11.boolean.opBoolean","COPY",EDGE,{"derivedFrom":makeQuery(id+"F11.opExtrude","SWEPT_EDGE",EDGE,{"disambiguationData":[OSD([sQuery(id+"F10.wireOp",EDGE,"E9.bottom"),sQuery(id+"F10.wireOp",EDGE,"E9.left")])]})});
            var Q12;
            Q12=makeQuery(id+"F17.boolean.opBoolean","COPY",EDGE,{"derivedFrom":makeQuery(id+"F17.opExtrude","SWEPT_EDGE",EDGE,{"disambiguationData":[OSD([sQuery(id+"F16.wireOp",EDGE,"E12.top"),sQuery(id+"F16.wireOp",EDGE,"E12.left")])]})});
            var Q13;
            Q13=makeQuery(id+"F19.boolean.opBoolean","COPY",EDGE,{"derivedFrom":makeQuery(id+"F19.opExtrude","SWEPT_EDGE",EDGE,{"disambiguationData":[OSD([sQuery(id+"F18.wireOp",EDGE,"E13.top"),sQuery(id+"F18.wireOp",EDGE,"E13.left")])]})});
            var Q14;
            Q14=makeQuery(id+"F21.boolean.opBoolean","COPY",EDGE,{"derivedFrom":makeQuery(id+"F21.opExtrude","SWEPT_EDGE",EDGE,{"disambiguationData":[OSD([sQuery(id+"F20.wireOp",EDGE,"E14.top"),sQuery(id+"F20.wireOp",EDGE,"E14.left")])]})});
            var Q15;
            Q15=makeQuery(id+"F23.boolean.opBoolean","COPY",EDGE,{"derivedFrom":makeQuery(id+"F23.opExtrude","SWEPT_EDGE",EDGE,{"disambiguationData":[OSD([sQuery(id+"F22.wireOp",EDGE,"E15.top"),sQuery(id+"F22.wireOp",EDGE,"E15.left")])]})});
            var Q16;
            Q16=makeQuery(id+"F25.boolean.opBoolean","COPY",EDGE,{"derivedFrom":makeQuery(id+"F25.opExtrude","SWEPT_EDGE",EDGE,{"disambiguationData":[OSD([sQuery(id+"F24.wireOp",EDGE,"E16.top"),sQuery(id+"F24.wireOp",EDGE,"E16.left")])]})});
            var Q17;
            Q17=makeQuery(id+"F27.boolean.opBoolean","COPY",EDGE,{"derivedFrom":makeQuery(id+"F27.opExtrude","SWEPT_EDGE",EDGE,{"disambiguationData":[OSD([sQuery(id+"F26.wireOp",EDGE,"E17.top"),sQuery(id+"F26.wireOp",EDGE,"E17.left")])]})});
            var Q18;
            Q18=makeQuery(id+"F19.boolean.opBoolean","COPY",EDGE,{"derivedFrom":makeQuery(id+"F19.opExtrude","SWEPT_EDGE",EDGE,{"disambiguationData":[OSD([sQuery(id+"F18.wireOp",EDGE,"E13.top"),sQuery(id+"F18.wireOp",EDGE,"E13.right")])]})});
            var Q19;
            Q19=makeQuery(id+"F21.boolean.opBoolean","COPY",EDGE,{"derivedFrom":makeQuery(id+"F21.opExtrude","SWEPT_EDGE",EDGE,{"disambiguationData":[OSD([sQuery(id+"F20.wireOp",EDGE,"E14.top"),sQuery(id+"F20.wireOp",EDGE,"E14.right")])]})});
            var Q20;
            Q20=makeQuery(id+"F23.boolean.opBoolean","COPY",EDGE,{"derivedFrom":makeQuery(id+"F23.opExtrude","SWEPT_EDGE",EDGE,{"disambiguationData":[OSD([sQuery(id+"F22.wireOp",EDGE,"E15.top"),sQuery(id+"F22.wireOp",EDGE,"E15.right")])]})});
            var Q21;
            Q21=makeQuery(id+"F25.boolean.opBoolean","COPY",EDGE,{"derivedFrom":makeQuery(id+"F25.opExtrude","SWEPT_EDGE",EDGE,{"disambiguationData":[OSD([sQuery(id+"F24.wireOp",EDGE,"E16.top"),sQuery(id+"F24.wireOp",EDGE,"E16.right")])]})});
            var Q22;
            Q22=makeQuery(id+"F27.boolean.opBoolean","COPY",EDGE,{"derivedFrom":makeQuery(id+"F27.opExtrude","SWEPT_EDGE",EDGE,{"disambiguationData":[OSD([sQuery(id+"F26.wireOp",EDGE,"E17.top"),sQuery(id+"F26.wireOp",EDGE,"E17.right")])]})});
            var Q23;
            Q23=makeQuery(id+"F17.boolean.opBoolean","COPY",EDGE,{"derivedFrom":makeQuery(id+"F17.opExtrude","SWEPT_EDGE",EDGE,{"disambiguationData":[OSD([sQuery(id+"F16.wireOp",EDGE,"E12.top"),sQuery(id+"F16.wireOp",EDGE,"E12.right")])]})});
            fillet(context, id + "F96", {"entities" : qUnion([Q0, Q1, Q2, Q3, Q4, Q5, Q6, Q7, Q8, Q9, Q10, Q11, Q12, Q13, Q14, Q15, Q16, Q17, Q18, Q19, Q20, Q21, Q22, Q23]), "radius" : 5 * mm, "tangentPropagation" : true, "allowEdgeOverflow" : false});
        }
        {
            var Q0;
            Q0=makeQuery(id+"F95.boolean.opBoolean","MERGE",FACE,{"derivedFrom":[makeQuery(id+"F1.opExtrude","CAP_FACE",FACE,{"disambiguationData":[OSD([sQuery(id+"F0.wireOp",EDGE,"E0"),sQuery(id+"F0.wireOp",EDGE,"E1"),sQuery(id+"F0.wireOp",EDGE,"E2"),sQuery(id+"F0.wireOp",EDGE,"E3")])],"isStart":true}),makeQuery(id+"F95.opExtrude","CAP_FACE",FACE,{"disambiguationData":[OSD([sQuery(id+"F94.wireOp",EDGE,"E53"),sQuery(id+"F94.wireOp",EDGE,"E54")])],"isStart":true})]});
            var sketch = newSketch(context, id + "F97", { "sketchPlane" : qUnion([Q0])});
            skCircle(sketch, "E55", {"center": v(-19.54, 71.15) * mm, "radius": 1.95 * mm});
            skSolve(sketch);
        }
        {
            var Q0;
            Q0 = qSketchRegion(id + "F97", true);
            extrude(context, id + "F98", {"entities" : qUnion([Q0]), "operationType" : NewBodyOperationType.REMOVE, "oppositeDirection" : true, "depth" : 10 * mm, "offsetDistance" : 25 * mm});
        }
        {
            var Q0;
            Q0=makeQuery(id+"F95.boolean.opBoolean","MERGE",FACE,{"derivedFrom":[makeQuery(id+"F1.opExtrude","CAP_FACE",FACE,{"disambiguationData":[OSD([sQuery(id+"F0.wireOp",EDGE,"E0"),sQuery(id+"F0.wireOp",EDGE,"E1"),sQuery(id+"F0.wireOp",EDGE,"E2"),sQuery(id+"F0.wireOp",EDGE,"E3")])],"isStart":true}),makeQuery(id+"F95.opExtrude","CAP_FACE",FACE,{"disambiguationData":[OSD([sQuery(id+"F94.wireOp",EDGE,"E53"),sQuery(id+"F94.wireOp",EDGE,"E54")])],"isStart":true})]});
            var sketch = newSketch(context, id + "F99", { "sketchPlane" : qUnion([Q0])});
            skEllipse(sketch, "E56", {"center": v(-15.57, 74.53) * mm, "majorRadius": 2.5 * mm, "minorRadius": 1.5 * mm, "majorAxis": v(0.8, 0.6)});
            skCircle(sketch, "E57.0", {"center": v(-19.54, 71.15) * mm, "radius": 1.95 * mm});
            skEllipse(sketch, "E58.1.0", {"center": v(-20.48, 76.27) * mm, "majorRadius": 2.5 * mm, "minorRadius": 1.5 * mm, "majorAxis": v(-0.11, 1)});
            skEllipse(sketch, "E58.2.0", {"center": v(-24.44, 72.9) * mm, "majorRadius": 2.5 * mm, "minorRadius": 1.5 * mm, "majorAxis": v(-0.92, 0.4)});
            skEllipse(sketch, "E58.3.0", {"center": v(-23.5, 67.77) * mm, "majorRadius": 2.5 * mm, "minorRadius": 1.5 * mm, "majorAxis": v(-0.8, -0.6)});
            skEllipse(sketch, "E58.4.0", {"center": v(-18.6, 66.03) * mm, "majorRadius": 2.5 * mm, "minorRadius": 1.5 * mm, "majorAxis": v(0.11, -1)});
            skEllipse(sketch, "E58.5.0", {"center": v(-14.63, 69.4) * mm, "majorRadius": 2.5 * mm, "minorRadius": 1.5 * mm, "majorAxis": v(0.92, -0.4)});
            skSolve(sketch);
        }
        {
            var Q0;
            Q0 = qSketchRegion(id + "F99", true);
            extrude(context, id + "F100", {"entities" : qUnion([Q0]), "operationType" : NewBodyOperationType.REMOVE, "endBound" : BoundingType.THROUGH_ALL, "oppositeDirection" : true, "depth" : 25 * mm, "offsetDistance" : 25 * mm});
        }
        {
            var Q0;
            Q0=makeQuery(id+"F95.boolean.opBoolean","MERGE",FACE,{"derivedFrom":[makeQuery(id+"F1.opExtrude","CAP_FACE",FACE,{"disambiguationData":[OSD([sQuery(id+"F0.wireOp",EDGE,"E0"),sQuery(id+"F0.wireOp",EDGE,"E1"),sQuery(id+"F0.wireOp",EDGE,"E2"),sQuery(id+"F0.wireOp",EDGE,"E3")])],"isStart":true}),makeQuery(id+"F95.opExtrude","CAP_FACE",FACE,{"disambiguationData":[OSD([sQuery(id+"F94.wireOp",EDGE,"E53"),sQuery(id+"F94.wireOp",EDGE,"E54")])],"isStart":true})]});
            var sketch = newSketch(context, id + "F101", { "sketchPlane" : qUnion([Q0])});
            skCircle(sketch, "E59", {"center": v(-38.21, 62.72) * mm, "radius": 1.04 * mm});
            skSolve(sketch);
        }
        {
            var Q0;
            Q0 = qSketchRegion(id + "F101", true);
            extrude(context, id + "F102", {"entities" : qUnion([Q0]), "operationType" : NewBodyOperationType.REMOVE, "endBound" : BoundingType.THROUGH_ALL, "oppositeDirection" : true, "depth" : 25 * mm, "offsetDistance" : 25 * mm});
        }
        {
            var Q0;
            Q0=makeQuery(id+"F95.boolean.opBoolean","MERGE",FACE,{"derivedFrom":[makeQuery(id+"F1.opExtrude","CAP_FACE",FACE,{"disambiguationData":[OSD([sQuery(id+"F0.wireOp",EDGE,"E0"),sQuery(id+"F0.wireOp",EDGE,"E1"),sQuery(id+"F0.wireOp",EDGE,"E2"),sQuery(id+"F0.wireOp",EDGE,"E3")])],"isStart":true}),makeQuery(id+"F95.opExtrude","CAP_FACE",FACE,{"disambiguationData":[OSD([sQuery(id+"F94.wireOp",EDGE,"E53"),sQuery(id+"F94.wireOp",EDGE,"E54")])],"isStart":true})]});
            var sketch = newSketch(context, id + "F103", { "sketchPlane" : qUnion([Q0])});
            skEllipse(sketch, "E60", {"center": v(-38.2, 65.9) * mm, "majorRadius": 1.67 * mm, "minorRadius": 0.73 * mm, "majorAxis": v(0, 1)});
            skCircle(sketch, "E61.0", {"center": v(-38.21, 62.72) * mm, "radius": 1.04 * mm});
            skEllipse(sketch, "E62.1.0", {"center": v(-40.95, 64.33) * mm, "majorRadius": 1.67 * mm, "minorRadius": 0.73 * mm, "majorAxis": v(-0.87, 0.5)});
            skEllipse(sketch, "E62.2.0", {"center": v(-40.97, 61.15) * mm, "majorRadius": 1.67 * mm, "minorRadius": 0.73 * mm, "majorAxis": v(-0.87, -0.5)});
            skEllipse(sketch, "E62.3.0", {"center": v(-38.23, 59.55) * mm, "majorRadius": 1.67 * mm, "minorRadius": 0.73 * mm, "majorAxis": v(0, -1)});
            skEllipse(sketch, "E62.4.0", {"center": v(-35.47, 61.12) * mm, "majorRadius": 1.67 * mm, "minorRadius": 0.73 * mm, "majorAxis": v(0.87, -0.5)});
            skEllipse(sketch, "E62.5.0", {"center": v(-35.45, 64.3) * mm, "majorRadius": 1.67 * mm, "minorRadius": 0.73 * mm, "majorAxis": v(0.87, 0.5)});
            skSolve(sketch);
        }
        {
            var Q0;
            Q0 = qSketchRegion(id + "F103", true);
            extrude(context, id + "F104", {"entities" : qUnion([Q0]), "operationType" : NewBodyOperationType.REMOVE, "endBound" : BoundingType.THROUGH_ALL, "oppositeDirection" : true, "depth" : 25 * mm, "offsetDistance" : 25 * mm});
        }
        {
            var Q0;
            Q0=makeQuery(id+"F95.boolean.opBoolean","MERGE",FACE,{"derivedFrom":[makeQuery(id+"F1.opExtrude","CAP_FACE",FACE,{"disambiguationData":[OSD([sQuery(id+"F0.wireOp",EDGE,"E0"),sQuery(id+"F0.wireOp",EDGE,"E1"),sQuery(id+"F0.wireOp",EDGE,"E2"),sQuery(id+"F0.wireOp",EDGE,"E3")])],"isStart":true}),makeQuery(id+"F95.opExtrude","CAP_FACE",FACE,{"disambiguationData":[OSD([sQuery(id+"F94.wireOp",EDGE,"E53"),sQuery(id+"F94.wireOp",EDGE,"E54")])],"isStart":true})]});
            var sketch = newSketch(context, id + "F105", { "sketchPlane" : qUnion([Q0])});
            skCircle(sketch, "E63", {"center": v(9.4, 72.13) * mm, "radius": 2.03 * mm});
            skSolve(sketch);
        }
        {
            var Q0;
            Q0 = qSketchRegion(id + "F105", true);
            extrude(context, id + "F106", {"entities" : qUnion([Q0]), "operationType" : NewBodyOperationType.REMOVE, "endBound" : BoundingType.THROUGH_ALL, "oppositeDirection" : true, "depth" : 25 * mm, "offsetDistance" : 25 * mm});
        }
        {
            var Q0;
            Q0=makeQuery(id+"F95.boolean.opBoolean","MERGE",FACE,{"derivedFrom":[makeQuery(id+"F1.opExtrude","CAP_FACE",FACE,{"disambiguationData":[OSD([sQuery(id+"F0.wireOp",EDGE,"E0"),sQuery(id+"F0.wireOp",EDGE,"E1"),sQuery(id+"F0.wireOp",EDGE,"E2"),sQuery(id+"F0.wireOp",EDGE,"E3")])],"isStart":true}),makeQuery(id+"F95.opExtrude","CAP_FACE",FACE,{"disambiguationData":[OSD([sQuery(id+"F94.wireOp",EDGE,"E53"),sQuery(id+"F94.wireOp",EDGE,"E54")])],"isStart":true})]});
            var sketch = newSketch(context, id + "F107", { "sketchPlane" : qUnion([Q0])});
            skEllipse(sketch, "E64", {"center": v(11.32, 77.12) * mm, "majorRadius": 2.5 * mm, "minorRadius": 1.48 * mm, "majorAxis": v(-0.42, -0.9)});
            skCircle(sketch, "E65.0", {"center": v(9.4, 72.13) * mm, "radius": 2.03 * mm});
            skEllipse(sketch, "E66.1.0", {"center": v(6.03, 76.29) * mm, "majorRadius": 2.5 * mm, "minorRadius": 1.48 * mm, "majorAxis": v(0.58, -0.81)});
            skEllipse(sketch, "E66.2.0", {"center": v(4.1, 71.3) * mm, "majorRadius": 2.5 * mm, "minorRadius": 1.48 * mm, "majorAxis": v(1, 0.1)});
            skEllipse(sketch, "E66.3.0", {"center": v(7.47, 67.14) * mm, "majorRadius": 2.5 * mm, "minorRadius": 1.48 * mm, "majorAxis": v(0.42, 0.9)});
            skEllipse(sketch, "E66.4.0", {"center": v(12.75, 67.97) * mm, "majorRadius": 2.5 * mm, "minorRadius": 1.48 * mm, "majorAxis": v(-0.58, 0.81)});
            skEllipse(sketch, "E66.5.0", {"center": v(14.68, 72.96) * mm, "majorRadius": 2.5 * mm, "minorRadius": 1.48 * mm, "majorAxis": v(-1, -0.1)});
            skSolve(sketch);
        }
        {
            var Q0;
            Q0 = qSketchRegion(id + "F107", true);
            extrude(context, id + "F108", {"entities" : qUnion([Q0]), "operationType" : NewBodyOperationType.REMOVE, "endBound" : BoundingType.THROUGH_ALL, "oppositeDirection" : true, "depth" : 25 * mm, "offsetDistance" : 25 * mm});
        }
        {
            var Q0;
            Q0=makeQuery(id+"F95.boolean.opBoolean","MERGE",FACE,{"derivedFrom":[makeQuery(id+"F1.opExtrude","CAP_FACE",FACE,{"disambiguationData":[OSD([sQuery(id+"F0.wireOp",EDGE,"E0"),sQuery(id+"F0.wireOp",EDGE,"E1"),sQuery(id+"F0.wireOp",EDGE,"E2"),sQuery(id+"F0.wireOp",EDGE,"E3")])],"isStart":true}),makeQuery(id+"F95.opExtrude","CAP_FACE",FACE,{"disambiguationData":[OSD([sQuery(id+"F94.wireOp",EDGE,"E53"),sQuery(id+"F94.wireOp",EDGE,"E54")])],"isStart":true})]});
            var sketch = newSketch(context, id + "F109", { "sketchPlane" : qUnion([Q0])});
            skCircle(sketch, "E67", {"center": v(-4.46, 59.43) * mm, "radius": 1.06 * mm});
            skSolve(sketch);
        }
        {
            var Q0;
            Q0 = qSketchRegion(id + "F109", true);
            extrude(context, id + "F110", {"entities" : qUnion([Q0]), "operationType" : NewBodyOperationType.REMOVE, "endBound" : BoundingType.THROUGH_ALL, "oppositeDirection" : true, "depth" : 25 * mm, "offsetDistance" : 25 * mm});
        }
        {
            var Q0;
            Q0=makeQuery(id+"F95.boolean.opBoolean","MERGE",FACE,{"derivedFrom":[makeQuery(id+"F1.opExtrude","CAP_FACE",FACE,{"disambiguationData":[OSD([sQuery(id+"F0.wireOp",EDGE,"E0"),sQuery(id+"F0.wireOp",EDGE,"E1"),sQuery(id+"F0.wireOp",EDGE,"E2"),sQuery(id+"F0.wireOp",EDGE,"E3")])],"isStart":true}),makeQuery(id+"F95.opExtrude","CAP_FACE",FACE,{"disambiguationData":[OSD([sQuery(id+"F94.wireOp",EDGE,"E53"),sQuery(id+"F94.wireOp",EDGE,"E54")])],"isStart":true})]});
            var sketch = newSketch(context, id + "F111", { "sketchPlane" : qUnion([Q0])});
            skEllipse(sketch, "E68", {"center": v(-3.88, 62.43) * mm, "majorRadius": 1.54 * mm, "minorRadius": 0.8 * mm, "majorAxis": v(-0.4, -0.92)});
            skCircle(sketch, "E69.0", {"center": v(-4.46, 59.43) * mm, "radius": 1.06 * mm});
            skEllipse(sketch, "E70.1.0", {"center": v(-6.76, 61.44) * mm, "majorRadius": 1.54 * mm, "minorRadius": 0.8 * mm, "majorAxis": v(0.6, -0.8)});
            skEllipse(sketch, "E70.2.0", {"center": v(-7.35, 58.44) * mm, "majorRadius": 1.54 * mm, "minorRadius": 0.8 * mm, "majorAxis": v(1, 0.1)});
            skEllipse(sketch, "E70.3.0", {"center": v(-5.05, 56.43) * mm, "majorRadius": 1.54 * mm, "minorRadius": 0.8 * mm, "majorAxis": v(0.4, 0.92)});
            skEllipse(sketch, "E70.4.0", {"center": v(-2.16, 57.42) * mm, "majorRadius": 1.54 * mm, "minorRadius": 0.8 * mm, "majorAxis": v(-0.6, 0.8)});
            skEllipse(sketch, "E70.5.0", {"center": v(-1.57, 60.42) * mm, "majorRadius": 1.54 * mm, "minorRadius": 0.8 * mm, "majorAxis": v(-1, -0.1)});
            skSolve(sketch);
        }
        {
            var Q0;
            Q0 = qSketchRegion(id + "F111", true);
            extrude(context, id + "F112", {"entities" : qUnion([Q0]), "operationType" : NewBodyOperationType.REMOVE, "endBound" : BoundingType.THROUGH_ALL, "oppositeDirection" : true, "depth" : 25 * mm, "offsetDistance" : 25 * mm});
        }
        {
            var Q0;
            Q0=makeQuery(id+"F95.boolean.opBoolean","MERGE",FACE,{"derivedFrom":[makeQuery(id+"F1.opExtrude","CAP_FACE",FACE,{"disambiguationData":[OSD([sQuery(id+"F0.wireOp",EDGE,"E0"),sQuery(id+"F0.wireOp",EDGE,"E1"),sQuery(id+"F0.wireOp",EDGE,"E2"),sQuery(id+"F0.wireOp",EDGE,"E3")])],"isStart":true}),makeQuery(id+"F95.opExtrude","CAP_FACE",FACE,{"disambiguationData":[OSD([sQuery(id+"F94.wireOp",EDGE,"E53"),sQuery(id+"F94.wireOp",EDGE,"E54")])],"isStart":true})]});
            var sketch = newSketch(context, id + "F113", { "sketchPlane" : qUnion([Q0])});
            skCircle(sketch, "E71", {"center": v(25.3, 65.27) * mm, "radius": 0.76 * mm});
            skSolve(sketch);
        }
        {
            var Q0;
            Q0 = qSketchRegion(id + "F113", true);
            extrude(context, id + "F114", {"entities" : qUnion([Q0]), "operationType" : NewBodyOperationType.REMOVE, "endBound" : BoundingType.THROUGH_ALL, "oppositeDirection" : true, "depth" : 25 * mm, "offsetDistance" : 25 * mm});
        }
        {
            var Q0;
            Q0=makeQuery(id+"F95.boolean.opBoolean","MERGE",FACE,{"derivedFrom":[makeQuery(id+"F1.opExtrude","CAP_FACE",FACE,{"disambiguationData":[OSD([sQuery(id+"F0.wireOp",EDGE,"E0"),sQuery(id+"F0.wireOp",EDGE,"E1"),sQuery(id+"F0.wireOp",EDGE,"E2"),sQuery(id+"F0.wireOp",EDGE,"E3")])],"isStart":true}),makeQuery(id+"F95.opExtrude","CAP_FACE",FACE,{"disambiguationData":[OSD([sQuery(id+"F94.wireOp",EDGE,"E53"),sQuery(id+"F94.wireOp",EDGE,"E54")])],"isStart":true})]});
            var sketch = newSketch(context, id + "F115", { "sketchPlane" : qUnion([Q0])});
            skEllipse(sketch, "E72", {"center": v(26.53, 67.38) * mm, "majorRadius": 1.33 * mm, "minorRadius": 0.68 * mm, "majorAxis": v(-0.55, -0.83)});
            skCircle(sketch, "E73.0", {"center": v(25.3, 65.27) * mm, "radius": 0.76 * mm});
            skEllipse(sketch, "E74.1.0", {"center": v(24.09, 67.38) * mm, "majorRadius": 1.33 * mm, "minorRadius": 0.68 * mm, "majorAxis": v(0.45, -0.9)});
            skEllipse(sketch, "E74.2.0", {"center": v(22.87, 65.27) * mm, "majorRadius": 1.33 * mm, "minorRadius": 0.68 * mm, "majorAxis": v(1, -0.06)});
            skEllipse(sketch, "E74.3.0", {"center": v(24.09, 63.16) * mm, "majorRadius": 1.33 * mm, "minorRadius": 0.68 * mm, "majorAxis": v(0.55, 0.83)});
            skEllipse(sketch, "E74.4.0", {"center": v(26.53, 63.16) * mm, "majorRadius": 1.33 * mm, "minorRadius": 0.68 * mm, "majorAxis": v(-0.45, 0.9)});
            skEllipse(sketch, "E74.5.0", {"center": v(27.75, 65.27) * mm, "majorRadius": 1.33 * mm, "minorRadius": 0.68 * mm, "majorAxis": v(-1, 0.06)});
            skSolve(sketch);
        }
        {
            var Q0;
            Q0 = qSketchRegion(id + "F115", true);
            extrude(context, id + "F116", {"entities" : qUnion([Q0]), "operationType" : NewBodyOperationType.REMOVE, "endBound" : BoundingType.THROUGH_ALL, "oppositeDirection" : true, "depth" : 25 * mm, "offsetDistance" : 25 * mm});
        }
    });
